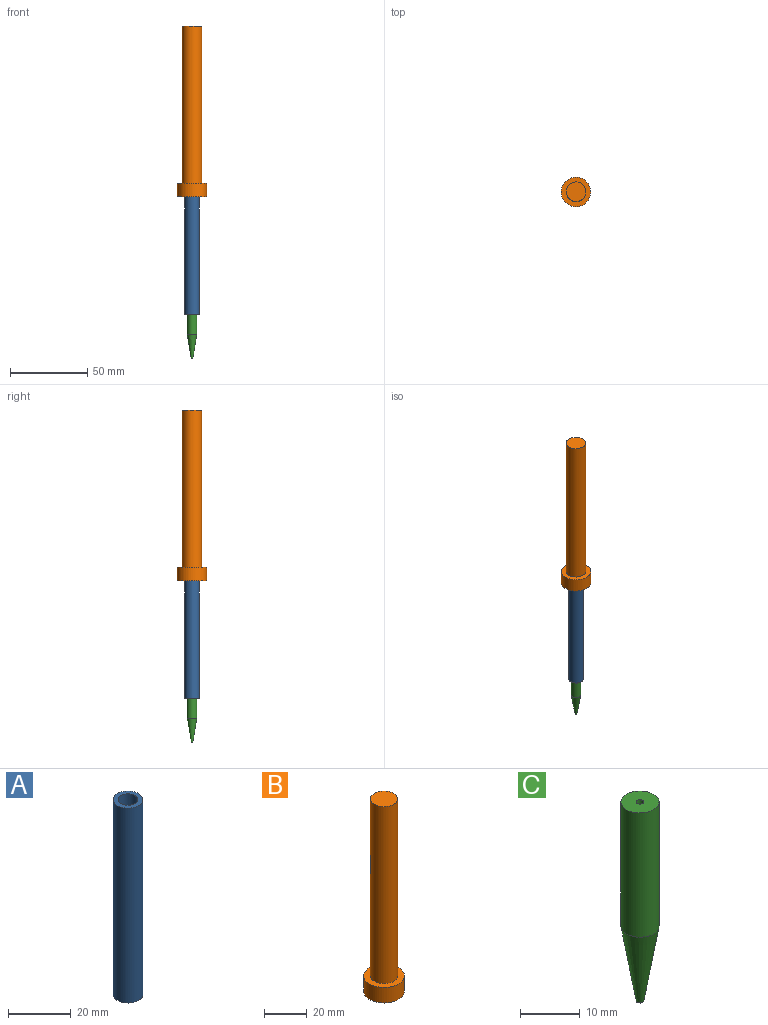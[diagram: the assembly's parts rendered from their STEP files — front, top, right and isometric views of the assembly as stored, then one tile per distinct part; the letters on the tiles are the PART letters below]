
ASSEMBLY  parts=3 mates=2
PART A: 4 faces, bbox 9.5x9.5x76.2 mm
  f0: cylinder r=4.76mm len=76.2mm, axis (0,0,-1), area 2280.2mm2, adj f1,f2
  f1: plane 9.53x9.53mm, normal (0,0,1), area 39.6mm2, adj f0,f3
  f2: plane 9.53x9.53mm, normal (0,0,-1), area 39.6mm2, adj f0,f3
  f3: cylinder r=3.17mm len=76.2mm, axis (0,0,1), area 1520.1mm2, adj f1,f2
PART B: 5 faces, bbox 19.1x19.1x110.5 mm
  f0: cylinder r=9.53mm len=19.05mm, axis (0,0,-1), area 532mm2, adj f1,f2
  f1: plane 19.05x19.05mm, normal (0,0,1), area 158.3mm2, adj f0,f3
  f2: plane 19.05x19.05mm, normal (0,0,-1), area 285mm2, adj f0
  f3: cylinder r=6.35mm len=101.6mm, axis (0,0,-1), area 4053.7mm2, adj f1,f4
  f4: plane 12.7x12.7mm, normal (0,0,1), area 126.7mm2, adj f3
PART C: 4 faces, bbox 6.4x6.4x40.6 mm
  f0: cylinder r=3.17mm len=25.4mm, axis (0,0,-1), area 506.7mm2, adj f1,f2
  f1: plane 6.35x6.35mm, normal (0,0,1), area 30.4mm2, adj f0,f3
  f2: cone r=3.17mm half-angle=9.5deg, axis (0,0,1), area 184.9mm2, adj f0,f3
  f3: cylinder r=0.64mm len=40.64mm, axis (0,0,1), area 162.1mm2, adj f1,f2
PLACE A t=(0,0,-76.2)mm
PLACE B at identity
PLACE C t=(0,0,-88.9)mm
MATE fastened C.f0 <-> A.f0  axis (0,0,-1) through (0,0,-76.2)mm
MATE fastened B.f0 <-> A.f0  axis (0,0,-1) through (0,0,0)mm
